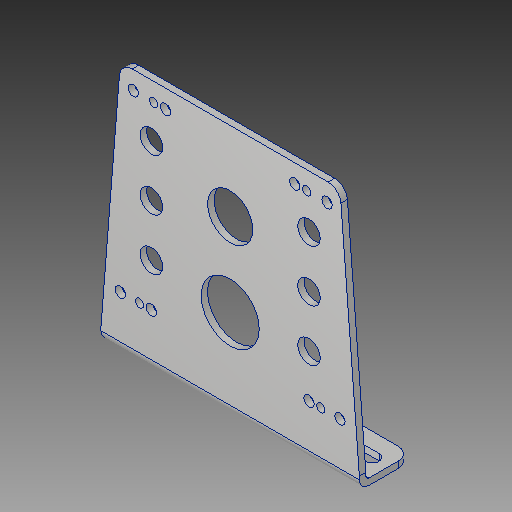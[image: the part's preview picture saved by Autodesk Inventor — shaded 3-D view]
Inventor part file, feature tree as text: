
AUTODESK INVENTOR PART (.ipt)
format: ipt  version: 2018 (Build 220112000, 112)  size: 164,864 bytes
history: native  units: in
note: dims shown in document units (in); Inventor stores cm internally (conversion verified against a paired STEP export)
features: fillet x1
ambient origin geometry x8: Origin, YZ Plane, XZ Plane, XY Plane, X Axis, Y Axis, Z Axis, Center Point
bodies: Solid1 (feature_tree)
feature tree (1):
  fillet  "Fillet6"  [1 undecoded]
note: 1 required parameter value undecoded (feature->parameter linkage not recoverable at this tier; creation-order binding heuristic only, values carry confidence <= 0.55)
